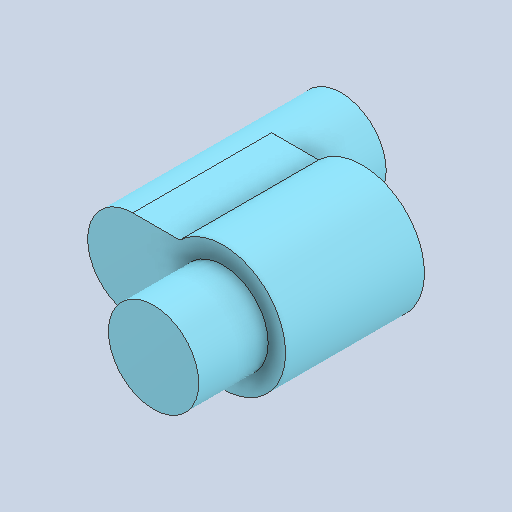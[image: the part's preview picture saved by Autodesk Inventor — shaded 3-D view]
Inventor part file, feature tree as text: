
AUTODESK INVENTOR PART (.ipt)
format: ipt  version: 2022 (Build 260153000, 153)  size: 124,416 bytes
history: native  units: in
note: dims shown in document units (in); Inventor stores cm internally (conversion verified against a paired STEP export)
features: other x3, sketch x2
ambient origin geometry x8: Origin, YZ Plane, XZ Plane, XY Plane, X Axis, Y Axis, Z Axis, Center Point
bodies: Solid1 (feature_tree)
feature tree (5):
  other  "Component28.ipt"
  other  "Solid1::Component28.ipt"
  other  "TaggingFeature1"
  sketch  "Sketch2"  dims[d0=0.3937in]
  sketch  "Sketch3"
